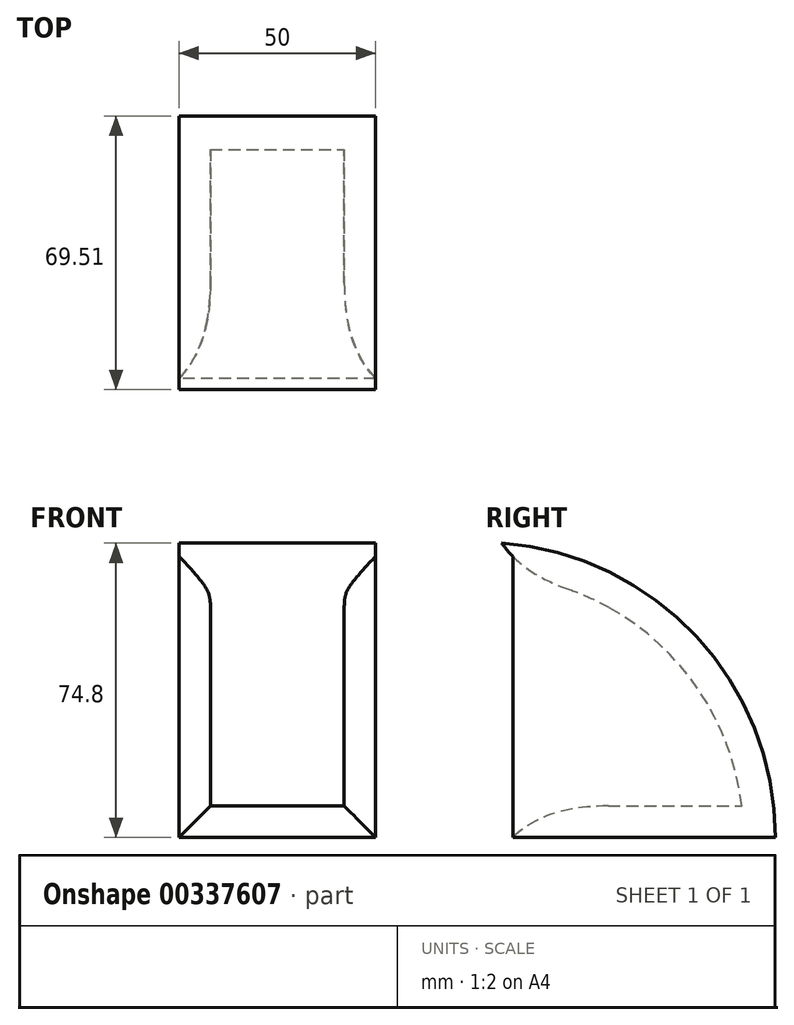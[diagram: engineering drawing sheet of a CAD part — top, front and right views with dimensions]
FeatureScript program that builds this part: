
annotation { "Feature Type Name" : "Feature", "Feature Type Description" : "" }
export const myFeature = defineFeature(function(context is Context, id is Id, definition is map)
    precondition{}
    {
        {
            var Q0;
            Q0=qCreatedBy(makeId("Front.planeOp"),FACE);
            var sketch = newSketch(context, id + "F0", { "sketchPlane" : qUnion([Q0])});
            skLineSegment(sketch, "E0.bottom", {"start": v(25, -37.5) * mm, "end": v(-25, -37.5) * mm});
            skLineSegment(sketch, "E0.top", {"start": v(25, 37.5) * mm, "end": v(-25, 37.5) * mm});
            skLineSegment(sketch, "E0.left", {"start": v(25, -37.5) * mm, "end": v(25, 37.5) * mm});
            skLineSegment(sketch, "E0.right", {"start": v(-25, -37.5) * mm, "end": v(-25, 37.5) * mm});
            skPoint(sketch, "E0.middle", {"position": v(0, 0) * mm});
            skSolve(sketch);
        }
        {
            var Q0;
            Q0 = qSketchRegion(id + "F0", true);
            var Q1;
            Q1=sQuery(id+"F0.wireOp",EDGE,"E0.bottom");
            revolve(context, id + "F1", {"entities" : qUnion([Q0]), "axis" : qUnion([Q1]), "revolveType" : RevolveType.ONE_DIRECTION, "angle" : 90 * degree});
        }
        {
            var Q0;
            Q0=makeQuery(id+"F1.opRevolve","CAP_FACE",FACE,{"disambiguationData":[OSD([sQuery(id+"F0.wireOp",EDGE,"E0.bottom"),sQuery(id+"F0.wireOp",EDGE,"E0.top"),sQuery(id+"F0.wireOp",EDGE,"E0.left"),sQuery(id+"F0.wireOp",EDGE,"E0.right")])],"isStart":true});
            shell(context, id + "F2", {"entities" : qUnion([Q0]), "thickness" : 8 * mm});
        }
        {
            var Q0;
            {var subQ0=sQuery(id+"F0.wireOp",EDGE,"E0.right");Q0=makeQuery(id+"F2.opShell","OFFSET_EDGE",EDGE,{"disambiguationData":[OSD([subQ0]),TDD([makeQuery(id+"F1.opRevolve","CAP_EDGE",EDGE,{"disambiguationData":[OSD([subQ0])],"isStart":true})])]});}
            var Q1;
            {var subQ0=sQuery(id+"F0.wireOp",EDGE,"E0.top");Q1=makeQuery(id+"F2.opShell","OFFSET_EDGE",EDGE,{"disambiguationData":[OSD([subQ0]),TDD([makeQuery(id+"F1.opRevolve","CAP_EDGE",EDGE,{"disambiguationData":[OSD([subQ0])],"isStart":true})])]});}
            var Q2;
            {var subQ0=sQuery(id+"F0.wireOp",EDGE,"E0.left");Q2=makeQuery(id+"F2.opShell","OFFSET_EDGE",EDGE,{"disambiguationData":[OSD([subQ0]),TDD([makeQuery(id+"F1.opRevolve","CAP_EDGE",EDGE,{"disambiguationData":[OSD([subQ0])],"isStart":true})])]});}
            var Q3;
            Q3=makeQuery(id+"F2.opShell","OFFSET_EDGE",EDGE,{"disambiguationData":[OSD([sQuery(id+"F0.wireOp",EDGE,"E0.bottom")])]});
            fillet(context, id + "F3", {"entities" : qUnion([Q0, Q1, Q2, Q3]), "radius" : 32.6 * mm, "tangentPropagation" : true, "rho" : 0.5, "crossSection" : FilletCrossSection.CONIC, "allowEdgeOverflow" : false});
        }
    });
